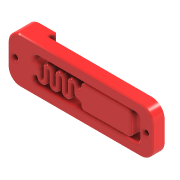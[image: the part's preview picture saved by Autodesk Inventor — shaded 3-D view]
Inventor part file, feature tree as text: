
AUTODESK INVENTOR PART (.ipt)
format: ipt  version: 2021 (Build 250183000, 183)  size: 299,008 bytes
history: native  units: mm
features: fillet x2, direct_edit x1, extrude x1, chamfer x1, sketch x1, move_body x1
ambient origin geometry x8: Origin, YZ Plane, XZ Plane, XY Plane, X Axis, Y Axis, Z Axis, Center Point
bodies: Volumenkörper2 (feature_tree), Body3 (feature_tree)
feature tree (7):
  direct_edit  "Direktbearbeitung1"
  extrude  "Extrusion1"  Depth=0.8mm
  fillet  "Rundung1"  Radius=1.0mm
  chamfer  "Fase1"  Distance=10.0mm
  fillet  "Rundung2"  Radius=0.8mm
  sketch  "Skizze1"  dims[d0=0.0mm d1=0.0mm d2=1.5mm d3=1.0mm d4=1.0mm d6=10.0mm d7=0.0mm d8=0.8mm d9=0.5mm d10=2.0mm d11=45.0deg d12=0.8mm]
  move_body  "Verschieben1"
